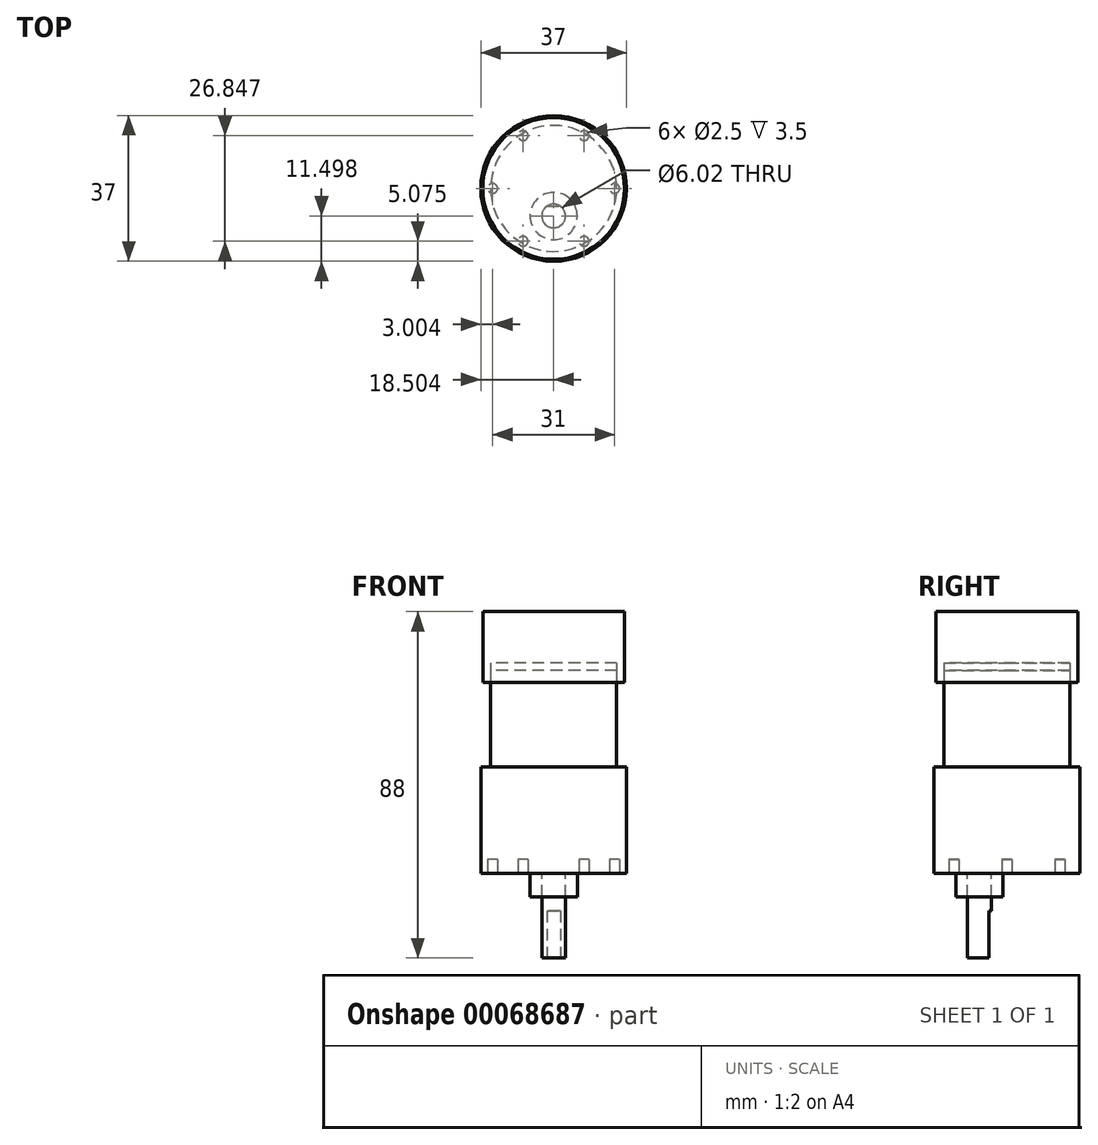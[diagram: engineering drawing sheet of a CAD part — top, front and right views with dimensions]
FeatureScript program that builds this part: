
annotation { "Feature Type Name" : "Feature", "Feature Type Description" : "" }
export const myFeature = defineFeature(function(context is Context, id is Id, definition is map)
    precondition{}
    {
        {
            var Q0;
            Q0=qCreatedBy(makeId("Top.planeOp"),FACE);
            var sketch = newSketch(context, id + "F0", { "sketchPlane" : qUnion([Q0])});
            skCircle(sketch, "E0", {"center": v(-57.04, -34.52) * mm, "radius": 3 * mm});
            skCircle(sketch, "E1", {"center": v(-57.04, -34.52) * mm, "radius": 6 * mm});
            skCircle(sketch, "E2", {"center": v(-57.04, -27.52) * mm, "radius": 18.5 * mm});
            skLineSegment(sketch, "E3", {"start": v(-41.54, -27.52) * mm, "end": v(-72.54, -27.52) * mm, "construction": true});
            skCircle(sketch, "E4", {"center": v(-41.54, -27.52) * mm, "radius": 1.25 * mm});
            skCircle(sketch, "E5.1.0", {"center": v(-49.29, -14.1) * mm, "radius": 1.25 * mm});
            skCircle(sketch, "E5.2.0", {"center": v(-64.79, -14.1) * mm, "radius": 1.25 * mm});
            skCircle(sketch, "E5.3.0", {"center": v(-72.54, -27.52) * mm, "radius": 1.25 * mm});
            skCircle(sketch, "E5.4.0", {"center": v(-64.79, -40.95) * mm, "radius": 1.25 * mm});
            skCircle(sketch, "E5.5.0", {"center": v(-49.29, -40.95) * mm, "radius": 1.25 * mm});
            skSolve(sketch);
        }
        {
            var Q0;
            Q0=makeQuery(id+"F0.imprint","IMPRINT",FACE,{"disambiguationData":[TD([[makeQuery(id+"F0.imprint","IMPRINT",EDGE,{"derivedFrom":sQuery(id+"F0.wireOp",EDGE,"E0")}),1.0]])]});
            extrude(context, id + "F1", {"entities" : qUnion([Q0]), "oppositeDirection" : true, "depth" : 21.5 * mm});
        }
        {
            var Q0;
            Q0=makeQuery(id+"F0.imprint","IMPRINT",FACE,{"disambiguationData":[TD([[makeQuery(id+"F0.imprint","IMPRINT",EDGE,{"derivedFrom":sQuery(id+"F0.wireOp",EDGE,"E0")}),-1.0]])]});
            extrude(context, id + "F2", {"entities" : qUnion([Q0]), "oppositeDirection" : true, "depth" : 6 * mm});
        }
        {
            var Q0;
            Q0=makeQuery(id+"F0.imprint","IMPRINT",FACE,{"disambiguationData":[TD([[makeQuery(id+"F0.imprint","IMPRINT",EDGE,{"derivedFrom":sQuery(id+"F0.wireOp",EDGE,"E0")}),-1.0]])]});
            var Q1;
            Q1=makeQuery(id+"F0.imprint","IMPRINT",FACE,{"disambiguationData":[TD([[makeQuery(id+"F0.imprint","IMPRINT",EDGE,{"derivedFrom":sQuery(id+"F0.wireOp",EDGE,"E0")}),1.0]])]});
            var Q2;
            Q2=makeQuery(id+"F0.imprint","IMPRINT",FACE,{"disambiguationData":[TD([[makeQuery(id+"F0.imprint","IMPRINT",EDGE,{"derivedFrom":sQuery(id+"F0.wireOp",EDGE,"E5.4.0")}),1.0]])]});
            var Q3;
            Q3=makeQuery(id+"F0.imprint","IMPRINT",FACE,{"disambiguationData":[TD([[makeQuery(id+"F0.imprint","IMPRINT",EDGE,{"derivedFrom":sQuery(id+"F0.wireOp",EDGE,"E1")}),-1.0]])]});
            var Q4;
            Q4=makeQuery(id+"F0.imprint","IMPRINT",FACE,{"disambiguationData":[TD([[makeQuery(id+"F0.imprint","IMPRINT",EDGE,{"derivedFrom":sQuery(id+"F0.wireOp",EDGE,"E5.5.0")}),1.0]])]});
            var Q5;
            Q5=makeQuery(id+"F0.imprint","IMPRINT",FACE,{"disambiguationData":[TD([[makeQuery(id+"F0.imprint","IMPRINT",EDGE,{"derivedFrom":sQuery(id+"F0.wireOp",EDGE,"E4")}),1.0]])]});
            var Q6;
            Q6=makeQuery(id+"F0.imprint","IMPRINT",FACE,{"disambiguationData":[TD([[makeQuery(id+"F0.imprint","IMPRINT",EDGE,{"derivedFrom":sQuery(id+"F0.wireOp",EDGE,"E5.1.0")}),1.0]])]});
            var Q7;
            Q7=makeQuery(id+"F0.imprint","IMPRINT",FACE,{"disambiguationData":[TD([[makeQuery(id+"F0.imprint","IMPRINT",EDGE,{"derivedFrom":sQuery(id+"F0.wireOp",EDGE,"E5.2.0")}),1.0]])]});
            var Q8;
            Q8=makeQuery(id+"F0.imprint","IMPRINT",FACE,{"disambiguationData":[TD([[makeQuery(id+"F0.imprint","IMPRINT",EDGE,{"derivedFrom":sQuery(id+"F0.wireOp",EDGE,"E5.3.0")}),1.0]])]});
            extrude(context, id + "F3", {"entities" : qUnion([Q0, Q1, Q2, Q3, Q4, Q5, Q6, Q7, Q8]), "depth" : 27 * mm});
        }
        {
            var Q0;
            Q0=makeQuery(id+"F0.imprint","IMPRINT",FACE,{"disambiguationData":[TD([[makeQuery(id+"F0.imprint","IMPRINT",EDGE,{"derivedFrom":sQuery(id+"F0.wireOp",EDGE,"E5.4.0")}),1.0]])]});
            var Q1;
            Q1=makeQuery(id+"F0.imprint","IMPRINT",FACE,{"disambiguationData":[TD([[makeQuery(id+"F0.imprint","IMPRINT",EDGE,{"derivedFrom":sQuery(id+"F0.wireOp",EDGE,"E5.5.0")}),1.0]])]});
            var Q2;
            Q2=makeQuery(id+"F0.imprint","IMPRINT",FACE,{"disambiguationData":[TD([[makeQuery(id+"F0.imprint","IMPRINT",EDGE,{"derivedFrom":sQuery(id+"F0.wireOp",EDGE,"E4")}),1.0]])]});
            var Q3;
            Q3=makeQuery(id+"F0.imprint","IMPRINT",FACE,{"disambiguationData":[TD([[makeQuery(id+"F0.imprint","IMPRINT",EDGE,{"derivedFrom":sQuery(id+"F0.wireOp",EDGE,"E5.1.0")}),1.0]])]});
            var Q4;
            Q4=makeQuery(id+"F0.imprint","IMPRINT",FACE,{"disambiguationData":[TD([[makeQuery(id+"F0.imprint","IMPRINT",EDGE,{"derivedFrom":sQuery(id+"F0.wireOp",EDGE,"E5.2.0")}),1.0]])]});
            var Q5;
            Q5=makeQuery(id+"F0.imprint","IMPRINT",FACE,{"disambiguationData":[TD([[makeQuery(id+"F0.imprint","IMPRINT",EDGE,{"derivedFrom":sQuery(id+"F0.wireOp",EDGE,"E5.3.0")}),1.0]])]});
            extrude(context, id + "F4", {"entities" : qUnion([Q0, Q1, Q2, Q3, Q4, Q5]), "depth" : 3.5 * mm});
        }
        {
            var Q0;
            Q0=makeQuery(id+"F4.opExtrude","SWEPT_BODY",BODY,{"disambiguationData":[OSD([sQuery(id+"F0.wireOp",EDGE,"E5.5.0")])]});
            var Q1;
            Q1=makeQuery(id+"F4.opExtrude","SWEPT_BODY",BODY,{"disambiguationData":[OSD([sQuery(id+"F0.wireOp",EDGE,"E5.3.0")])]});
            var Q2;
            Q2=makeQuery(id+"F4.opExtrude","SWEPT_BODY",BODY,{"disambiguationData":[OSD([sQuery(id+"F0.wireOp",EDGE,"E5.4.0")])]});
            var Q3;
            Q3=makeQuery(id+"F4.opExtrude","SWEPT_BODY",BODY,{"disambiguationData":[OSD([sQuery(id+"F0.wireOp",EDGE,"E5.2.0")])]});
            var Q4;
            Q4=makeQuery(id+"F4.opExtrude","SWEPT_BODY",BODY,{"disambiguationData":[OSD([sQuery(id+"F0.wireOp",EDGE,"E5.1.0")])]});
            var Q5;
            Q5=makeQuery(id+"F4.opExtrude","SWEPT_BODY",BODY,{"disambiguationData":[OSD([sQuery(id+"F0.wireOp",EDGE,"E4")])]});
            var Q6;
            Q6=makeQuery(id+"F3.opExtrude","SWEPT_BODY",BODY,{"disambiguationData":[OSD([sQuery(id+"F0.wireOp",EDGE,"E2")])]});
            booleanBodies(context, id + "F5", {"operationType" : BooleanOperationType.SUBTRACTION, "tools" : qUnion([Q0, Q1, Q2, Q3, Q4, Q5]), "targets" : qUnion([Q6])});
        }
        {
            var Q0;
            Q0=makeQuery(id+"F1.opExtrude","CAP_FACE",FACE,{"disambiguationData":[OSD([sQuery(id+"F0.wireOp",EDGE,"E0")])],"isStart":false});
            var sketch = newSketch(context, id + "F6", { "sketchPlane" : qUnion([Q0])});
            skLineSegment(sketch, "E6", {"start": v(-57.04, 32.03) * mm, "end": v(-57.04, 37.53) * mm, "construction": true});
            skLineSegment(sketch, "E7", {"start": v(-58.73, 32.03) * mm, "end": v(-55.35, 32.03) * mm});
            skArc(sketch, "E8.0", {"start": v(-58.73, 32.03) * mm, "mid": v(-57.04, 31.51) * mm, "end": v(-55.35, 32.03) * mm});
            skSolve(sketch);
        }
        {
            var Q0;
            Q0 = qSketchRegion(id + "F6", true);
            extrude(context, id + "F7", {"entities" : qUnion([Q0]), "operationType" : NewBodyOperationType.REMOVE, "oppositeDirection" : true, "depth" : 12 * mm});
        }
        {
            var Q0;
            Q0=makeQuery(id+"F3.opExtrude","CAP_FACE",FACE,{"disambiguationData":[OSD([sQuery(id+"F0.wireOp",EDGE,"E2")])],"isStart":false});
            var sketch = newSketch(context, id + "F8", { "sketchPlane" : qUnion([Q0])});
            skCircle(sketch, "E9", {"center": v(-57.04, -27.52) * mm, "radius": 16 * mm});
            skSolve(sketch);
        }
        {
            var Q0;
            Q0 = qSketchRegion(id + "F8", true);
            extrude(context, id + "F9", {"entities" : qUnion([Q0]), "operationType" : NewBodyOperationType.ADD, "depth" : 24.5 * mm});
        }
        {
            var Q0;
            Q0=makeQuery(id+"F9.opExtrude","CAP_FACE",FACE,{"disambiguationData":[OSD([sQuery(id+"F8.wireOp",EDGE,"E9")])],"isStart":false});
            var sketch = newSketch(context, id + "F10", { "sketchPlane" : qUnion([Q0])});
            skCircle(sketch, "E10.0", {"center": v(-57.04, -27.52) * mm, "radius": 16 * mm});
            skSolve(sketch);
        }
        {
            var Q0;
            Q0 = qSketchRegion(id + "F10", true);
            extrude(context, id + "F11", {"entities" : qUnion([Q0]), "depth" : 2 * mm});
        }
        {
            var Q0;
            Q0=makeQuery(id+"F11.opExtrude","CAP_FACE",FACE,{"disambiguationData":[OSD([sQuery(id+"F10.wireOp",EDGE,"E10.0")])],"isStart":false});
            var sketch = newSketch(context, id + "F12", { "sketchPlane" : qUnion([Q0])});
            skCircle(sketch, "E11", {"center": v(-57.04, -27.52) * mm, "radius": 18 * mm});
            skSolve(sketch);
        }
        {
            var Q0;
            Q0 = qSketchRegion(id + "F12", true);
            extrude(context, id + "F13", {"entities" : qUnion([Q0]), "depth" : 13 * mm, "hasSecondDirection" : true, "secondDirectionOppositeDirection" : true, "secondDirectionDepth" : 5 * mm});
        }
    });
